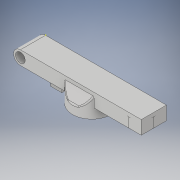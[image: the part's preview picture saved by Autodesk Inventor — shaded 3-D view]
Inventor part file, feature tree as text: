
AUTODESK INVENTOR PART (.ipt)
format: ipt  version: 2019 (Build 230136000, 136)  size: 249,856 bytes
history: native  units: in
note: dims shown in document units (in); Inventor stores cm internally (conversion verified against a paired STEP export)
features: sketch x9, extrude x5, chamfer x2, fillet x2
ambient origin geometry x8: Origin, YZ Plane, XZ Plane, XY Plane, X Axis, Y Axis, Z Axis, Center Point
bodies: Solid1 (feature_tree)
feature tree (18):
  extrude  "Extrusion1"  Depth=2.4606in
  extrude  "Extrusion2"  Depth=0.5118in TaperAngle=0.0deg
  extrude  "Extrusion3"  Depth=0.1969in TaperAngle=0.0deg
  sketch  "Sketch4"  dims[d9=2.2047in]
  chamfer  "Chamfer1"  Distance=0.1969in
  chamfer  "Chamfer2"  Distance=0.0787in Angle=120.0deg
  extrude  "Extrusion4"  Depth=0.0787in TaperAngle=0.0deg
  fillet  "Fillet2"  Radius=0.0394in
  fillet  "Fillet3"  Radius=0.0394in
  sketch  "Sketch6"  dims[d15=0.2559in]
  sketch  "Sketch7"  dims[d16=0.2559in d17=0.1181in d18=0.0787in d19=120.0deg]
  sketch  "Sketch8"  dims[d20=0.1181in d21=0.0787in d22=120.0deg d25=0.2362in d26=0.0in d28=0.0394in d29=0.0394in]
  sketch  "Sketch9"  dims[d30=1.3386in d32=0.2362in d33=0.1575in d34=0.4331in d35=0.1772in d36=0.0787in d37=0.0787in d39=0.1575in d41=0.0591in d42=0.1575in d43=0.0in]
  extrude  "Extrusion5"  Depth=0.0787in
  sketch  "Sketch1"  dims[d0=0.1969in d2=2.4606in]
  sketch  "Sketch2"  dims[d3=0.1378in d4=0.5118in d5=0.0in]
  sketch  "Sketch3"  dims[d6=0.5118in d7=0.1969in d8=0.0in]
  sketch  "Sketch5"  dims[d11=0.7874in d13=0.1969in d14=0.0in]
